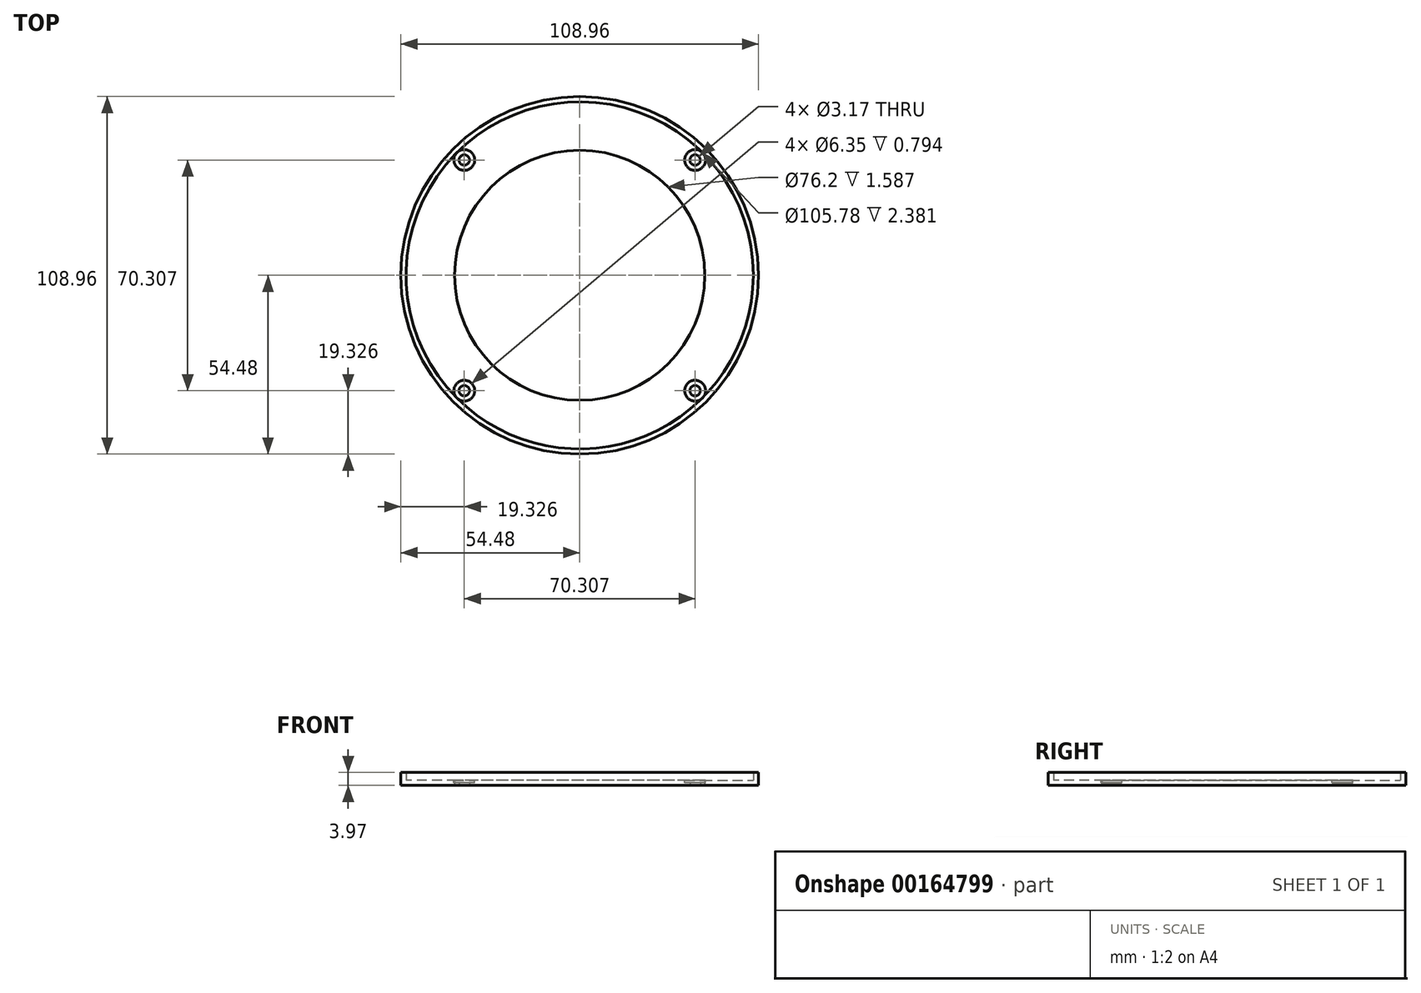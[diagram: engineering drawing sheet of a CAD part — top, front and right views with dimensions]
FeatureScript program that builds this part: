
annotation { "Feature Type Name" : "Feature", "Feature Type Description" : "" }
export const myFeature = defineFeature(function(context is Context, id is Id, definition is map)
    precondition{}
    {
        {
            var Q0;
            Q0=qCreatedBy(makeId("Top.planeOp"),FACE);
            var sketch = newSketch(context, id + "F0", { "sketchPlane" : qUnion([Q0])});
            skCircle(sketch, "E0", {"center": v(0, 0) * mm, "radius": 54.48 * mm});
            skCircle(sketch, "E1", {"center": v(0, 0) * mm, "radius": 38.1 * mm});
            skLineSegment(sketch, "E2.bottom", {"start": v(-35.15, 35.15) * mm, "end": v(35.15, 35.15) * mm, "construction": true});
            skLineSegment(sketch, "E2.top", {"start": v(-35.15, -35.15) * mm, "end": v(35.15, -35.15) * mm, "construction": true});
            skLineSegment(sketch, "E2.left", {"start": v(-35.15, 35.15) * mm, "end": v(-35.15, -35.15) * mm, "construction": true});
            skLineSegment(sketch, "E2.right", {"start": v(35.15, 35.15) * mm, "end": v(35.15, -35.15) * mm, "construction": true});
            skCircle(sketch, "E3", {"center": v(-35.15, 35.15) * mm, "radius": 1.59 * mm});
            skCircle(sketch, "E4", {"center": v(-35.15, -35.15) * mm, "radius": 1.59 * mm});
            skCircle(sketch, "E5", {"center": v(35.15, -35.15) * mm, "radius": 1.59 * mm});
            skCircle(sketch, "E6", {"center": v(35.15, 35.15) * mm, "radius": 1.59 * mm});
            skCircle(sketch, "E7", {"center": v(0, 0) * mm, "radius": 52.89 * mm, "construction": true});
            skCircle(sketch, "E8", {"center": v(35.15, -35.15) * mm, "radius": 3.18 * mm, "construction": true});
            skSolve(sketch);
        }
        {
            var Q0;
            Q0 = qSketchRegion(id + "F0", true);
            extrude(context, id + "F1", {"entities" : qUnion([Q0]), "depth" : 1.59 * mm});
        }
        {
            var Q0;
            Q0=makeQuery(id+"F1.opExtrude","CAP_FACE",FACE,{"disambiguationData":[OSD([sQuery(id+"F0.wireOp",EDGE,"E0"),sQuery(id+"F0.wireOp",EDGE,"E1"),sQuery(id+"F0.wireOp",EDGE,"E3"),sQuery(id+"F0.wireOp",EDGE,"E4"),sQuery(id+"F0.wireOp",EDGE,"E5"),sQuery(id+"F0.wireOp",EDGE,"E6")])],"isStart":false});
            var sketch = newSketch(context, id + "F2", { "sketchPlane" : qUnion([Q0])});
            skCircle(sketch, "E9", {"center": v(0, 0) * mm, "radius": 54.48 * mm});
            skCircle(sketch, "E10", {"center": v(0, 0) * mm, "radius": 52.89 * mm});
            skSolve(sketch);
        }
        {
            var Q0;
            Q0 = qSketchRegion(id + "F2", true);
            extrude(context, id + "F3", {"entities" : qUnion([Q0]), "operationType" : NewBodyOperationType.ADD, "depth" : 2.38 * mm});
        }
        {
            var Q0;
            Q0=makeQuery(id+"F1.opExtrude","CAP_FACE",FACE,{"disambiguationData":[OSD([sQuery(id+"F0.wireOp",EDGE,"E0"),sQuery(id+"F0.wireOp",EDGE,"E1"),sQuery(id+"F0.wireOp",EDGE,"E3"),sQuery(id+"F0.wireOp",EDGE,"E4"),sQuery(id+"F0.wireOp",EDGE,"E5"),sQuery(id+"F0.wireOp",EDGE,"E6")])],"isStart":false});
            var sketch = newSketch(context, id + "F4", { "sketchPlane" : qUnion([Q0])});
            skCircle(sketch, "E11", {"center": v(-35.15, 35.15) * mm, "radius": 3.18 * mm});
            skCircle(sketch, "E12", {"center": v(35.15, 35.15) * mm, "radius": 3.18 * mm});
            skCircle(sketch, "E13", {"center": v(35.15, -35.15) * mm, "radius": 3.18 * mm});
            skCircle(sketch, "E14", {"center": v(-35.15, -35.15) * mm, "radius": 3.17 * mm});
            skSolve(sketch);
        }
        {
            var Q0;
            Q0 = qSketchRegion(id + "F4", true);
            extrude(context, id + "F5", {"entities" : qUnion([Q0]), "operationType" : NewBodyOperationType.REMOVE, "oppositeDirection" : true, "depth" : 0.8 * mm});
        }
    });
